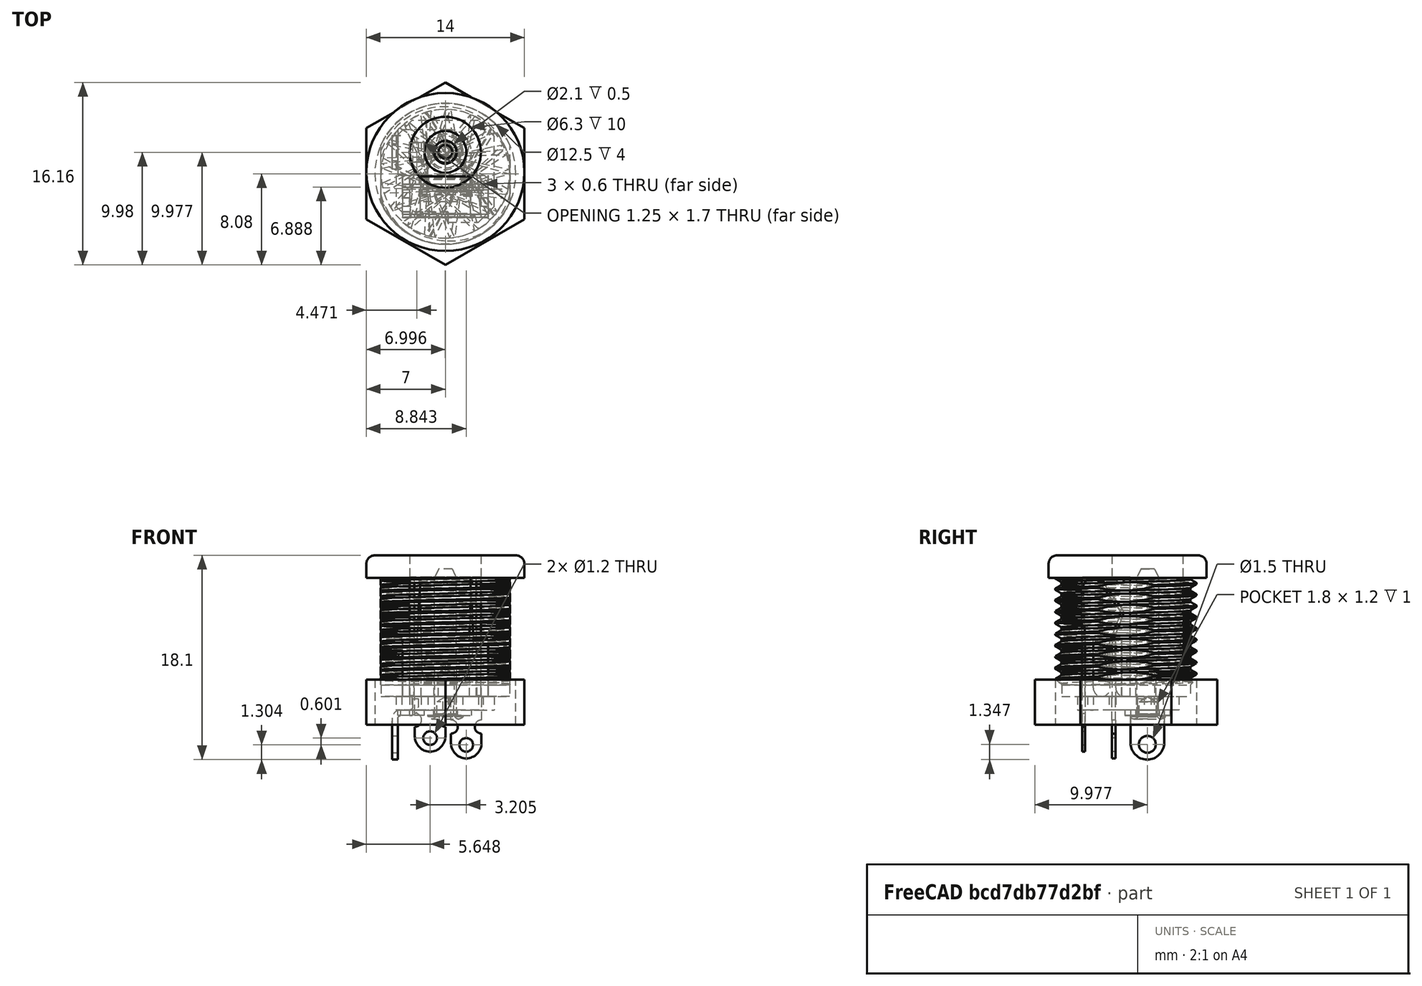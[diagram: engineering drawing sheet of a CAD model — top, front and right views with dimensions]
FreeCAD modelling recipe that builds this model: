
FCSTD DOCUMENT  (FreeCAD 0.19R17069 (Git))
Label: Lumberg_NEB_J_21_C
License: All rights reserved
LicenseURL: http://en.wikipedia.org/wiki/All_rights_reserved
objects: Part::Feature×1, Sketcher::SketchObject×1, PartDesign::Pad×1, PartDesign::Body×1
note: 5 computed .brp shape members not serialized (recipe doc carries the construction recipe); baked Part::Feature solids carry a one-line shape summary decoded from their .brp

FEATURE [Part::Feature] Part__Feature001  label="NEB/J 21 C"
  Placement = pos=(-1.6e-15,0,13) rot=(1,0,0;3.14159rad)
  shape: bbox 15.16 x 15.16 x 18.11 mm, 266 faces (baked)
FEATURE [Sketcher::SketchObject] Sketch
  MapMode = 5
  Support = -> [XY_Plane]
  sketch-geometry (8):
    g0: LineSegment StartX=0 StartY=8.0829 StartZ=0 EndX=-7 EndY=4.04145 EndZ=0
    g1: LineSegment StartX=-7 StartY=4.04145 StartZ=0 EndX=-7 EndY=-4.04145 EndZ=0
    g2: LineSegment StartX=-7 StartY=-4.04145 StartZ=0 EndX=-2.7e-15 EndY=-8.0829 EndZ=0
    g3: LineSegment StartX=-2.7e-15 StartY=-8.0829 StartZ=0 EndX=7 EndY=-4.04145 EndZ=0
    g4: LineSegment StartX=7 StartY=-4.04145 StartZ=0 EndX=7 EndY=4.04145 EndZ=0
    g5: LineSegment StartX=7 StartY=4.04145 StartZ=0 EndX=0 EndY=8.0829 EndZ=0
    g6: Circle [constr] CenterX=0 CenterY=0 CenterZ=0 NormalX=0 NormalY=0 NormalZ=1 AngleXU=0 Radius=8.0829
    g7: Circle CenterX=0 CenterY=0 CenterZ=0 NormalX=0 NormalY=0 NormalZ=1 AngleXU=0 Radius=6.25
  constraints (18):
    c: Coincident(g0,g1)
    c: Coincident(g1,g2)
    c: Coincident(g2,g3)
    c: Coincident(g3,g4)
    c: Coincident(g4,g5)
    c: Coincident(g5,g0)
    c: Equal(g0, g1-g5) x5
    c: PointOnObject(g0,g6)
    c: PointOnObject(g1,g6)
    c: PointOnObject(g2,g6)
    c: PointOnObject(g3,g6)
    c: PointOnObject(g4,g6)
    c: PointOnObject(g5,g6)
    c: Coincident(g6,g-1)
    c: PointOnObject(g5,g-2)
    c: DistanceX(g0,g4) = 14
    c: Coincident(g7,g-1)
    c: Radius(g7) = 6.25
FEATURE [PartDesign::Pad] Pad
  Length = 4
  Length2 = 100
  Profile = -> Sketch
  Type = 0
FEATURE [PartDesign::Body] Body  label="NEB/J 21 C Nut"
  Group = -> [Sketch,Pad]
  Origin = -> Origin
  Tip = -> Pad
